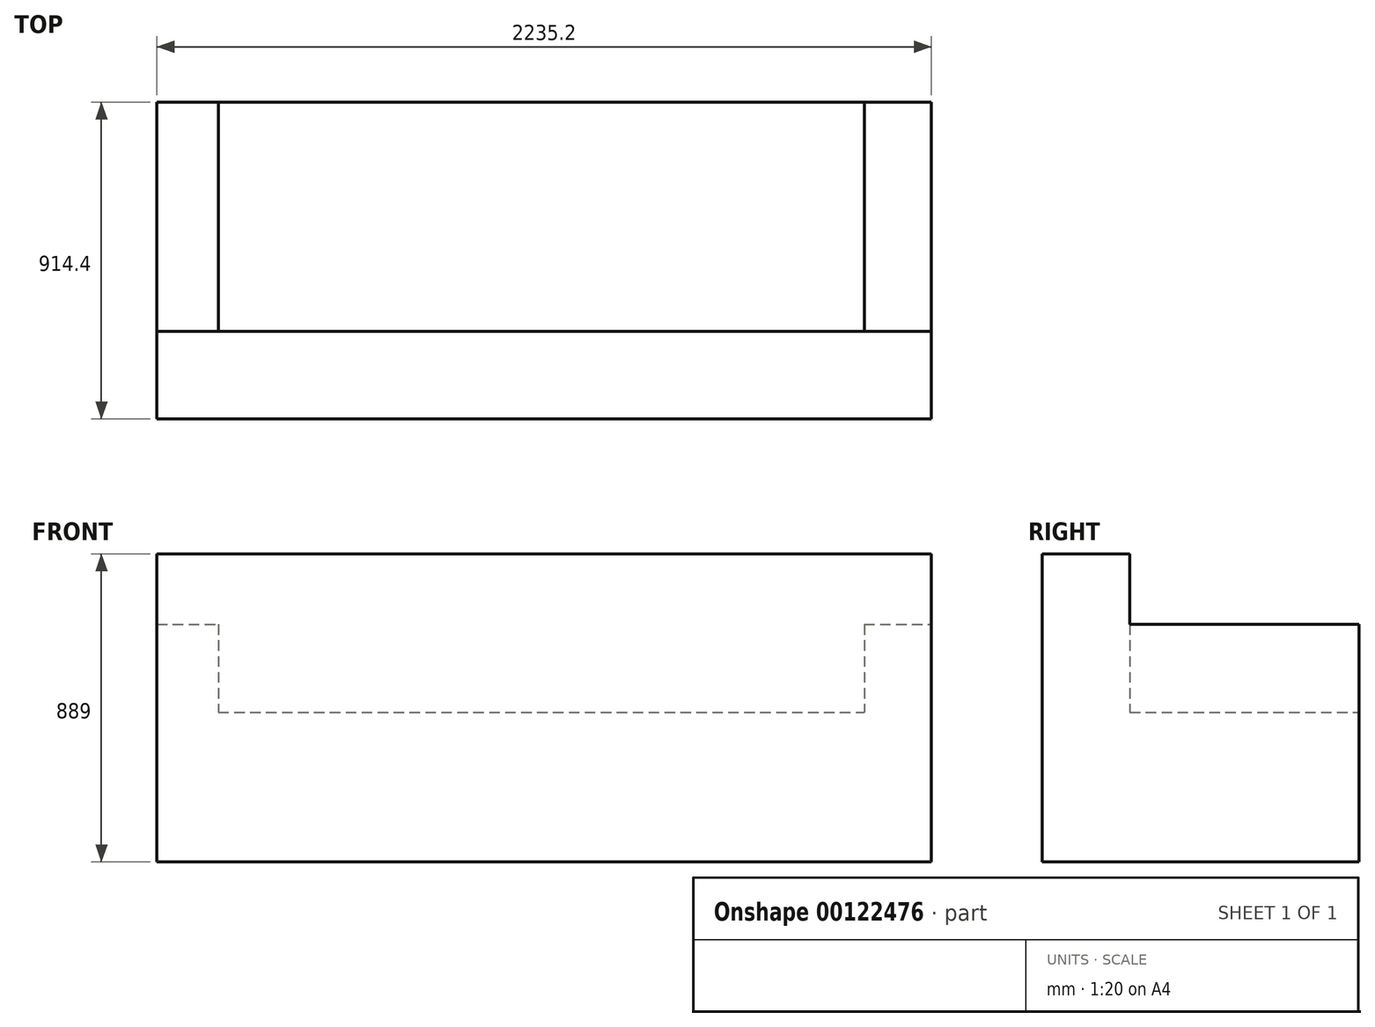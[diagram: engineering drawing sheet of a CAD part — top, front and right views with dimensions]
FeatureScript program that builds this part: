
annotation { "Feature Type Name" : "Feature", "Feature Type Description" : "" }
export const myFeature = defineFeature(function(context is Context, id is Id, definition is map)
    precondition{}
    {
        {
            var Q0;
            Q0=qCreatedBy(makeId("Top.planeOp"),FACE);
            var sketch = newSketch(context, id + "F0", { "sketchPlane" : qUnion([Q0])});
            skLineSegment(sketch, "E0.bottom", {"start": v(0, 0) * mm, "end": v(2235.2, 0) * mm});
            skLineSegment(sketch, "E0.top", {"start": v(0, -914.4) * mm, "end": v(2235.2, -914.4) * mm});
            skLineSegment(sketch, "E0.left", {"start": v(0, 0) * mm, "end": v(0, -914.4) * mm});
            skLineSegment(sketch, "E0.right", {"start": v(2235.2, 0) * mm, "end": v(2235.2, -914.4) * mm});
            skSolve(sketch);
        }
        {
            var Q0;
            Q0 = qSketchRegion(id + "F0", true);
            extrude(context, id + "F1", {"entities" : qUnion([Q0]), "depth" : 431.8 * mm});
        }
        {
            var Q0;
            Q0=makeQuery(id+"F1.opExtrude","CAP_FACE",FACE,{"disambiguationData":[OSD([sQuery(id+"F0.wireOp",EDGE,"E0.bottom"),sQuery(id+"F0.wireOp",EDGE,"E0.top"),sQuery(id+"F0.wireOp",EDGE,"E0.left"),sQuery(id+"F0.wireOp",EDGE,"E0.right")])],"isStart":false});
            var sketch = newSketch(context, id + "F2", { "sketchPlane" : qUnion([Q0])});
            skLineSegment(sketch, "E1.bottom", {"start": v(0, -914.4) * mm, "end": v(2235.2, -914.4) * mm});
            skLineSegment(sketch, "E1.top", {"start": v(0, -661.81) * mm, "end": v(2235.2, -661.81) * mm});
            skLineSegment(sketch, "E1.left", {"start": v(0, -914.4) * mm, "end": v(0, -661.81) * mm});
            skLineSegment(sketch, "E1.right", {"start": v(2235.2, -914.4) * mm, "end": v(2235.2, -661.81) * mm});
            skSolve(sketch);
        }
        {
            var Q0;
            Q0 = qSketchRegion(id + "F2", true);
            extrude(context, id + "F3", {"entities" : qUnion([Q0]), "operationType" : NewBodyOperationType.ADD, "depth" : 457.2 * mm});
        }
        {
            var Q0;
            Q0=makeQuery(id+"F1.opExtrude","CAP_FACE",FACE,{"disambiguationData":[OSD([sQuery(id+"F0.wireOp",EDGE,"E0.bottom"),sQuery(id+"F0.wireOp",EDGE,"E0.top"),sQuery(id+"F0.wireOp",EDGE,"E0.left"),sQuery(id+"F0.wireOp",EDGE,"E0.right")])],"isStart":false});
            var sketch = newSketch(context, id + "F4", { "sketchPlane" : qUnion([Q0])});
            skLineSegment(sketch, "E2.bottom", {"start": v(0, -661.81) * mm, "end": v(177.18, -661.81) * mm});
            skLineSegment(sketch, "E2.top", {"start": v(0, 0) * mm, "end": v(177.18, 0) * mm});
            skLineSegment(sketch, "E2.left", {"start": v(0, -661.81) * mm, "end": v(0, 0) * mm});
            skLineSegment(sketch, "E2.right", {"start": v(177.18, -661.81) * mm, "end": v(177.18, 0) * mm});
            skSolve(sketch);
        }
        {
            var Q0;
            Q0 = qSketchRegion(id + "F4", true);
            extrude(context, id + "F5", {"entities" : qUnion([Q0]), "operationType" : NewBodyOperationType.ADD, "depth" : 254 * mm});
        }
        {
            var Q0;
            Q0=makeQuery(id+"F1.opExtrude","CAP_FACE",FACE,{"disambiguationData":[OSD([sQuery(id+"F0.wireOp",EDGE,"E0.bottom"),sQuery(id+"F0.wireOp",EDGE,"E0.top"),sQuery(id+"F0.wireOp",EDGE,"E0.left"),sQuery(id+"F0.wireOp",EDGE,"E0.right")])],"isStart":false});
            var sketch = newSketch(context, id + "F6", { "sketchPlane" : qUnion([Q0])});
            skLineSegment(sketch, "E3.bottom", {"start": v(2235.2, -661.81) * mm, "end": v(2041.37, -661.81) * mm});
            skLineSegment(sketch, "E3.top", {"start": v(2235.2, 0) * mm, "end": v(2041.37, 0) * mm});
            skLineSegment(sketch, "E3.left", {"start": v(2235.2, -661.81) * mm, "end": v(2235.2, 0) * mm});
            skLineSegment(sketch, "E3.right", {"start": v(2041.37, -661.81) * mm, "end": v(2041.37, 0) * mm});
            skSolve(sketch);
        }
        {
            var Q0;
            Q0 = qSketchRegion(id + "F6", true);
            extrude(context, id + "F7", {"entities" : qUnion([Q0]), "operationType" : NewBodyOperationType.ADD, "depth" : 254 * mm});
        }
    });
